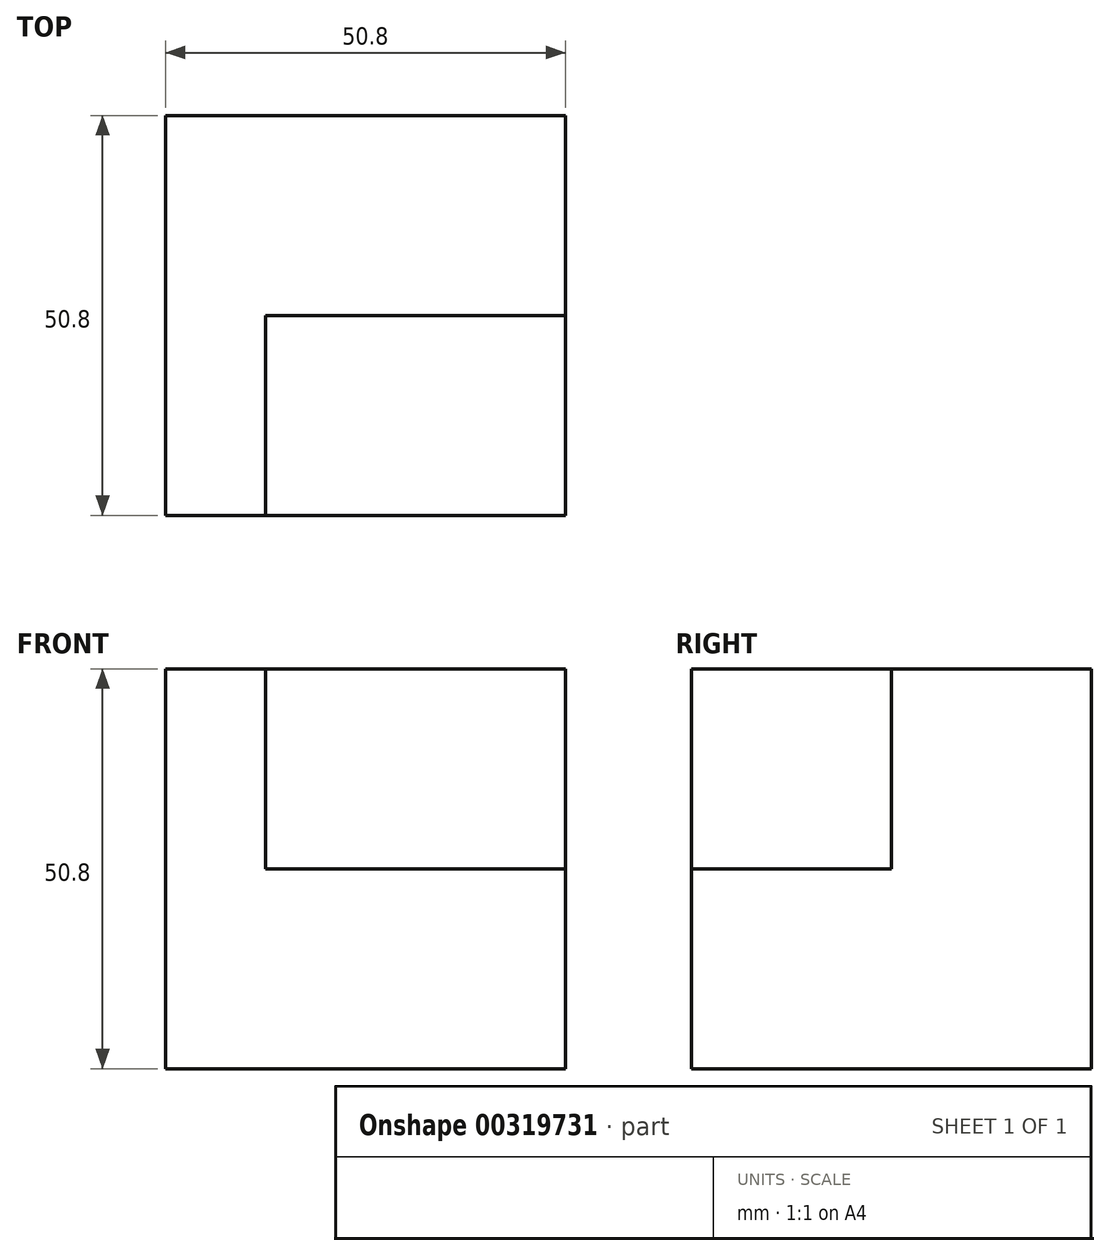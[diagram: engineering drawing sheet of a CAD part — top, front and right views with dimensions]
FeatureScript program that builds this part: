
annotation { "Feature Type Name" : "Feature", "Feature Type Description" : "" }
export const myFeature = defineFeature(function(context is Context, id is Id, definition is map)
    precondition{}
    {
        {
            var Q0;
            Q0=qCreatedBy(makeId("Front.planeOp"),FACE);
            var sketch = newSketch(context, id + "F0", { "sketchPlane" : qUnion([Q0])});
            skLineSegment(sketch, "E0", {"start": v(-34.5, 5.4) * mm, "end": v(-34.5, -45.4) * mm});
            skLineSegment(sketch, "E1", {"start": v(-34.5, -45.4) * mm, "end": v(16.3, -45.4) * mm});
            skLineSegment(sketch, "E2", {"start": v(16.3, -45.4) * mm, "end": v(16.3, 5.4) * mm});
            skLineSegment(sketch, "E3", {"start": v(16.3, 5.4) * mm, "end": v(-34.5, 5.4) * mm});
            skLineSegment(sketch, "E4", {"start": v(-21.8, 5.4) * mm, "end": v(-21.8, -20) * mm});
            skLineSegment(sketch, "E5", {"start": v(-21.8, -20) * mm, "end": v(16.3, -20) * mm});
            skSolve(sketch);
        }
        {
            var Q0;
            {var subQ4=sQuery(id+"F0.wireOp",EDGE,"E0");Q0=makeQuery(id+"F0.imprint","IMPRINT",FACE,{"disambiguationData":[TD([[makeQuery(id+"F0.imprint","IMPRINT",EDGE,{"derivedFrom":subQ4}),1.0]])]});}
            var Q1;
            {var subQ4=sQuery(id+"F0.wireOp",EDGE,"E4");Q1=makeQuery(id+"F0.imprint","IMPRINT",FACE,{"disambiguationData":[TD([[makeQuery(id+"F0.imprint","IMPRINT",EDGE,{"derivedFrom":subQ4}),1.0]])]});}
            extrude(context, id + "F1", {"entities" : qUnion([Q0, Q1]), "oppositeDirection" : true, "depth" : 50.8 * mm});
        }
        {
            var Q0;
            {var subQ4=sQuery(id+"F0.wireOp",EDGE,"E4");Q0=makeQuery(id+"F0.imprint","IMPRINT",FACE,{"disambiguationData":[TD([[makeQuery(id+"F0.imprint","IMPRINT",EDGE,{"derivedFrom":subQ4}),1.0]])]});}
            extrude(context, id + "F2", {"entities" : qUnion([Q0]), "operationType" : NewBodyOperationType.REMOVE, "oppositeDirection" : true, "depth" : 25.4 * mm});
        }
    });
